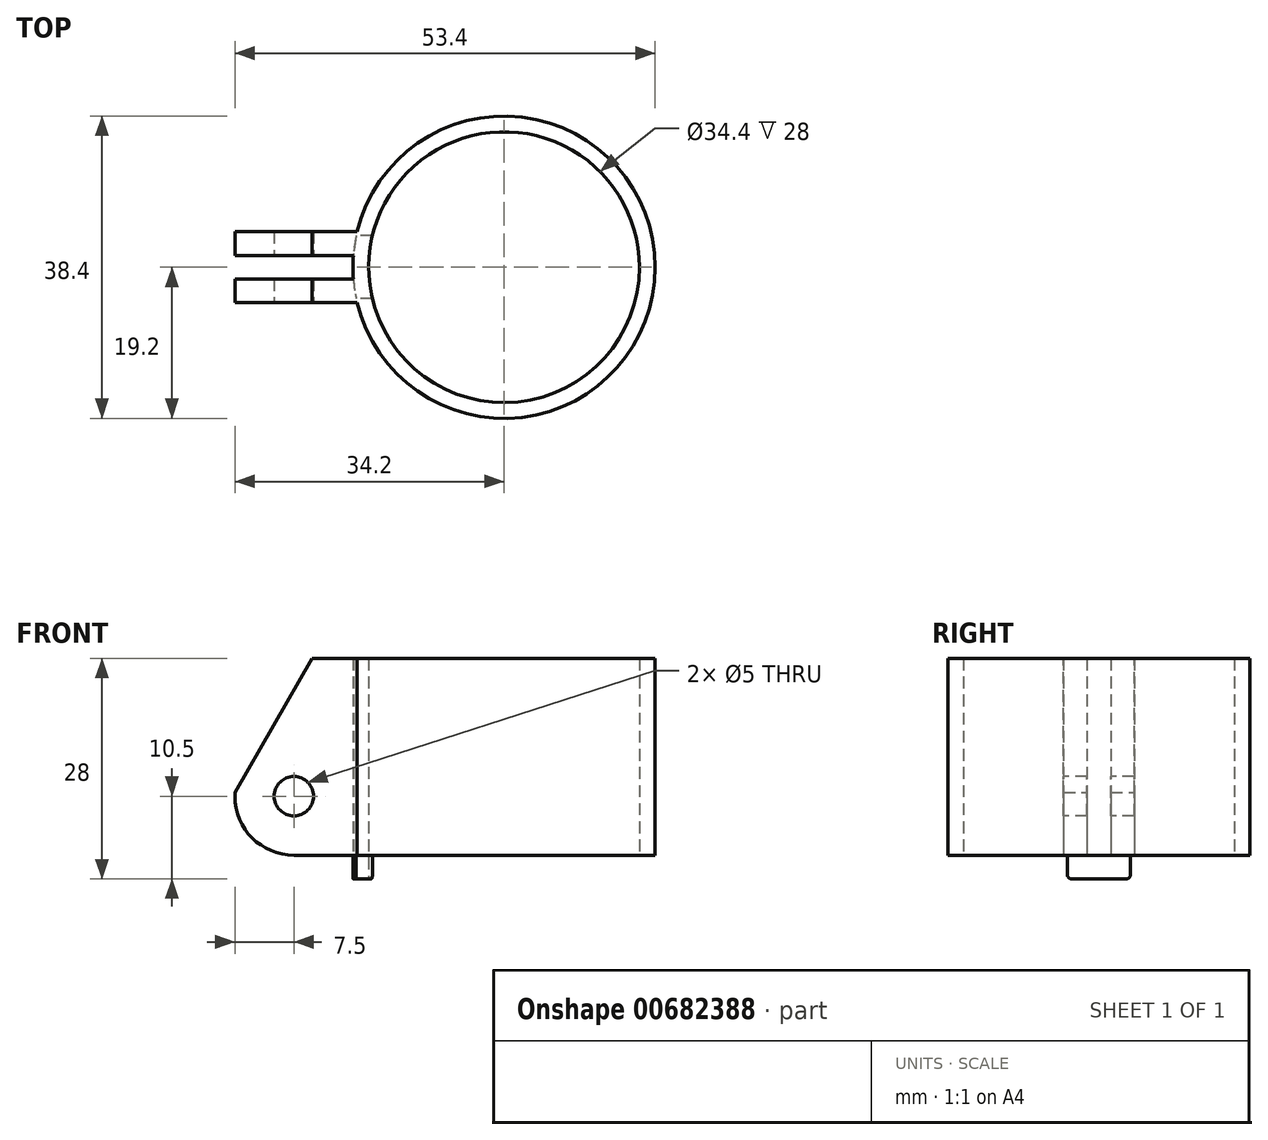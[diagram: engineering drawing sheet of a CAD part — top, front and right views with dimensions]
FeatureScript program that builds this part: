
annotation { "Feature Type Name" : "Feature", "Feature Type Description" : "" }
export const myFeature = defineFeature(function(context is Context, id is Id, definition is map)
    precondition{}
    {
        {
            var Q0;
            Q0=qCreatedBy(makeId("Top.planeOp"),FACE);
            var sketch = newSketch(context, id + "F0", { "sketchPlane" : qUnion([Q0])});
            skCircle(sketch, "E0", {"center": v(0, 0) * mm, "radius": 17.2 * mm});
            skCircle(sketch, "E1", {"center": v(0, 0) * mm, "radius": 19.2 * mm});
            skLineSegment(sketch, "E2", {"start": v(0, 0) * mm, "end": v(-19.2, 0) * mm, "construction": true});
            skLineSegment(sketch, "E3", {"start": v(-16.73, 4) * mm, "end": v(-18.78, 4) * mm});
            skLineSegment(sketch, "E4.MirrorCS", {"start": v(-16.73, -4) * mm, "end": v(-18.78, -4) * mm});
            skLineSegment(sketch, "E5", {"start": v(-19.2, 0) * mm, "end": v(-34.2, 0) * mm, "construction": true});
            skLineSegment(sketch, "E6", {"start": v(-19.14, 1.5) * mm, "end": v(-34.2, 1.5) * mm});
            skLineSegment(sketch, "E7", {"start": v(-18.67, 4.5) * mm, "end": v(-34.2, 4.5) * mm});
            skLineSegment(sketch, "E8", {"start": v(-34.2, 4.5) * mm, "end": v(-34.2, 1.5) * mm});
            skLineSegment(sketch, "E9.MirrorCS", {"start": v(-18.67, -4.5) * mm, "end": v(-34.2, -4.5) * mm});
            skLineSegment(sketch, "E10.MirrorCS", {"start": v(-34.2, -4.5) * mm, "end": v(-34.2, -1.5) * mm});
            skLineSegment(sketch, "E11.MirrorCS", {"start": v(-19.14, -1.5) * mm, "end": v(-34.2, -1.5) * mm});
            skSolve(sketch);
        }
        {
            var Q0;
            {var subQ0=sQuery(id+"F0.wireOp",EDGE,"E3");Q0=makeQuery(id+"F0.imprint","IMPRINT",FACE,{"disambiguationData":[TD([[makeQuery(id+"F0.imprint","IMPRINT",EDGE,{"derivedFrom":subQ0}),-1.0]])]});}
            var Q1;
            {var subQ0=sQuery(id+"F0.wireOp",EDGE,"E3");Q1=makeQuery(id+"F0.imprint","IMPRINT",FACE,{"disambiguationData":[TD([[makeQuery(id+"F0.imprint","IMPRINT",EDGE,{"derivedFrom":subQ0}),1.0]])]});}
            extrude(context, id + "F1", {"entities" : qUnion([Q0, Q1]), "depth" : 25 * mm, "offsetDistance" : 25 * mm});
        }
        {
            var Q0;
            {var subQ0=sQuery(id+"F0.wireOp",EDGE,"E3");Q0=makeQuery(id+"F0.imprint","IMPRINT",FACE,{"disambiguationData":[TD([[makeQuery(id+"F0.imprint","IMPRINT",EDGE,{"derivedFrom":subQ0}),1.0]])]});}
            extrude(context, id + "F2", {"entities" : qUnion([Q0]), "operationType" : NewBodyOperationType.ADD, "oppositeDirection" : true, "depth" : 3 * mm, "offsetDistance" : 25 * mm});
        }
        {
            var Q0;
            Q0=makeQuery(id+"F2.opExtrude","CAP_EDGE",EDGE,{"disambiguationData":[OSD([sQuery(id+"F0.wireOp",EDGE,"E3")])],"isStart":false});
            var Q1;
            Q1=makeQuery(id+"F2.opExtrude","CAP_EDGE",EDGE,{"disambiguationData":[OSD([sQuery(id+"F0.wireOp",EDGE,"E4.MirrorCS")])],"isStart":false});
            fillet(context, id + "F3", {"entities" : qUnion([Q0, Q1]), "radius" : 0.5 * mm, "tangentPropagation" : true, "allowEdgeOverflow" : false});
        }
        {
            var Q0;
            {var subQ1=sQuery(id+"F0.wireOp",EDGE,"E6");Q0=makeQuery(id+"F0.imprint","IMPRINT",FACE,{"disambiguationData":[TD([[makeQuery(id+"F0.imprint","IMPRINT",EDGE,{"derivedFrom":subQ1}),-1.0]])]});}
            var Q1;
            {var subQ0=sQuery(id+"F0.wireOp",EDGE,"E9.MirrorCS");Q1=makeQuery(id+"F0.imprint","IMPRINT",FACE,{"disambiguationData":[TD([[makeQuery(id+"F0.imprint","IMPRINT",EDGE,{"derivedFrom":subQ0}),-1.0]])]});}
            extrude(context, id + "F4", {"entities" : qUnion([Q0, Q1]), "operationType" : NewBodyOperationType.ADD, "depth" : 7.5 * mm, "offsetDistance" : 25 * mm});
        }
        {
            var Q0;
            Q0=makeQuery(id+"F4.opExtrude","CAP_EDGE",EDGE,{"disambiguationData":[OSD([sQuery(id+"F0.wireOp",EDGE,"E10.MirrorCS")])],"isStart":true});
            var Q1;
            Q1=makeQuery(id+"F4.opExtrude","CAP_EDGE",EDGE,{"disambiguationData":[OSD([sQuery(id+"F0.wireOp",EDGE,"E8")])],"isStart":true});
            fillet(context, id + "F5", {"entities" : qUnion([Q0, Q1]), "radius" : 7.5 * mm, "tangentPropagation" : true, "allowEdgeOverflow" : false});
        }
        {
            var Q0;
            Q0=makeQuery(id+"F4.opExtrude","CAP_FACE",FACE,{"disambiguationData":[OSD([sQuery(id+"F0.wireOp",EDGE,"E1"),sQuery(id+"F0.wireOp",EDGE,"E9.MirrorCS"),sQuery(id+"F0.wireOp",EDGE,"E10.MirrorCS"),sQuery(id+"F0.wireOp",EDGE,"E11.MirrorCS")])],"isStart":false});
            var Q1;
            Q1=makeQuery(id+"F4.opExtrude","CAP_FACE",FACE,{"disambiguationData":[OSD([sQuery(id+"F0.wireOp",EDGE,"E1"),sQuery(id+"F0.wireOp",EDGE,"E6"),sQuery(id+"F0.wireOp",EDGE,"E7"),sQuery(id+"F0.wireOp",EDGE,"E8")])],"isStart":false});
            var Q2;
            Q2=makeQuery(id+"F1.opExtrude","CAP_FACE",FACE,{"disambiguationData":[OSD([sQuery(id+"F0.wireOp",EDGE,"E0"),sQuery(id+"F0.wireOp",EDGE,"E1")])],"isStart":false});
            extrude(context, id + "F6", {"entities" : qUnion([Q0, Q1]), "operationType" : NewBodyOperationType.ADD, "endBound" : BoundingType.UP_TO_SURFACE, "depth" : 25 * mm, "endBoundEntityFace" : qUnion([Q2]), "offsetDistance" : 25 * mm});
        }
        {
            var Q0;
            Q0=makeQuery(id+"F6.opExtrude","CAP_EDGE",EDGE,{"disambiguationData":[OSD([sQuery(id+"F0.wireOp",EDGE,"E1"),sQuery(id+"F0.wireOp",EDGE,"E9.MirrorCS"),sQuery(id+"F0.wireOp",EDGE,"E10.MirrorCS"),sQuery(id+"F0.wireOp",EDGE,"E11.MirrorCS")])],"isStart":false});
            var Q1;
            Q1=makeQuery(id+"F6.opExtrude","CAP_EDGE",EDGE,{"disambiguationData":[OSD([sQuery(id+"F0.wireOp",EDGE,"E1"),sQuery(id+"F0.wireOp",EDGE,"E6"),sQuery(id+"F0.wireOp",EDGE,"E7"),sQuery(id+"F0.wireOp",EDGE,"E8")])],"isStart":false});
            chamfer(context, id + "F7", {"entities" : qUnion([Q0, Q1]), "chamferType" : ChamferType.OFFSET_ANGLE, "width" : 17 * mm, "oppositeDirection" : false, "angle" : 30 * degree, "tangentPropagation" : true});
        }
        {
            var Q0;
            {var subQ0=sQuery(id+"F0.wireOp",EDGE,"E9.MirrorCS");Q0=makeQuery(id+"F6.boolean.opBoolean","MERGE",FACE,{"derivedFrom":[makeQuery(id+"F4.opExtrude","SWEPT_FACE",FACE,{"disambiguationData":[OSD([subQ0])]}),makeQuery(id+"F6.opExtrude","SWEPT_FACE",FACE,{"disambiguationData":[OSD([subQ0])]})]});}
            var sketch = newSketch(context, id + "F8", { "sketchPlane" : qUnion([Q0])});
            skLineSegment(sketch, "E12", {"start": v(-34.2, 7.5) * mm, "end": v(-26.7, 7.5) * mm, "construction": true});
            skCircle(sketch, "E13", {"center": v(-26.7, 7.5) * mm, "radius": 2.5 * mm});
            skSolve(sketch);
        }
        {
            var Q0;
            Q0=makeQuery(id+"F8.imprint","IMPRINT",FACE,{"disambiguationData":[TD([[makeQuery(id+"F8.imprint","IMPRINT",EDGE,{"derivedFrom":sQuery(id+"F8.wireOp",EDGE,"E13")}),1.0]])]});
            extrude(context, id + "F9", {"entities" : qUnion([Q0]), "operationType" : NewBodyOperationType.REMOVE, "endBound" : BoundingType.THROUGH_ALL, "oppositeDirection" : true, "depth" : 25 * mm, "offsetDistance" : 25 * mm});
        }
    });
